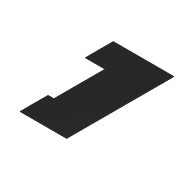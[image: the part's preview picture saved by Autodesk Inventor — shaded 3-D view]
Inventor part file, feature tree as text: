
AUTODESK INVENTOR PART (.ipt)
format: ipt  version: 2012 (Build 160160000, 160)  size: 87,552 bytes
history: native  units: in
note: dims shown in document units (in); Inventor stores cm internally (conversion verified against a paired STEP export)
features: extrude x3, sketch x3
ambient origin geometry x8: Origin, YZ Plane, XZ Plane, XY Plane, X Axis, Y Axis, Z Axis, Center Point
bodies: Solid1 (feature_tree)
feature tree (6):
  extrude  "Extrusion1"  Depth=0.125in
  extrude  "Extrusion2"  Depth=1.25in
  extrude  "Extrusion3"  Depth=23.0in TaperAngle=0.0deg
  sketch  "Sketch1"  dims[d0=10.0in d1=0.125in]
  sketch  "Sketch2"  dims[d2=23.0in d3=0.0in d4=1.25in]
  sketch  "Sketch3"  dims[d5=11.0in d7=23.0in d8=0.0in d9=3.0in d10=0.0in]
